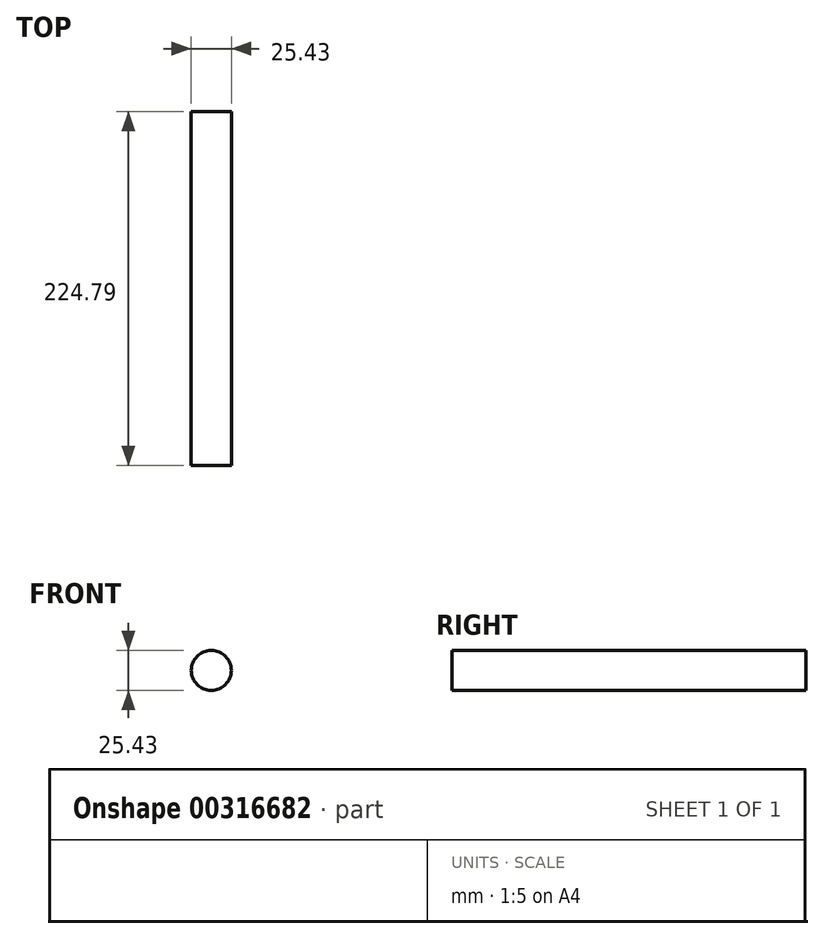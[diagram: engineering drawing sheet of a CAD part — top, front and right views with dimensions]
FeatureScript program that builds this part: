
annotation { "Feature Type Name" : "Feature", "Feature Type Description" : "" }
export const myFeature = defineFeature(function(context is Context, id is Id, definition is map)
    precondition{}
    {
        {
            var Q0;
            Q0=qCreatedBy(makeId("Front.planeOp"),FACE);
            var sketch = newSketch(context, id + "F0", { "sketchPlane" : qUnion([Q0])});
            skCircle(sketch, "E0", {"center": v(-21.12, 25.74) * mm, "radius": 12.71 * mm});
            skSolve(sketch);
        }
        {
            var Q0;
            Q0 = qSketchRegion(id + "F0", true);
            extrude(context, id + "F1", {"entities" : qUnion([Q0]), "depth" : 224.79 * mm});
        }
    });
